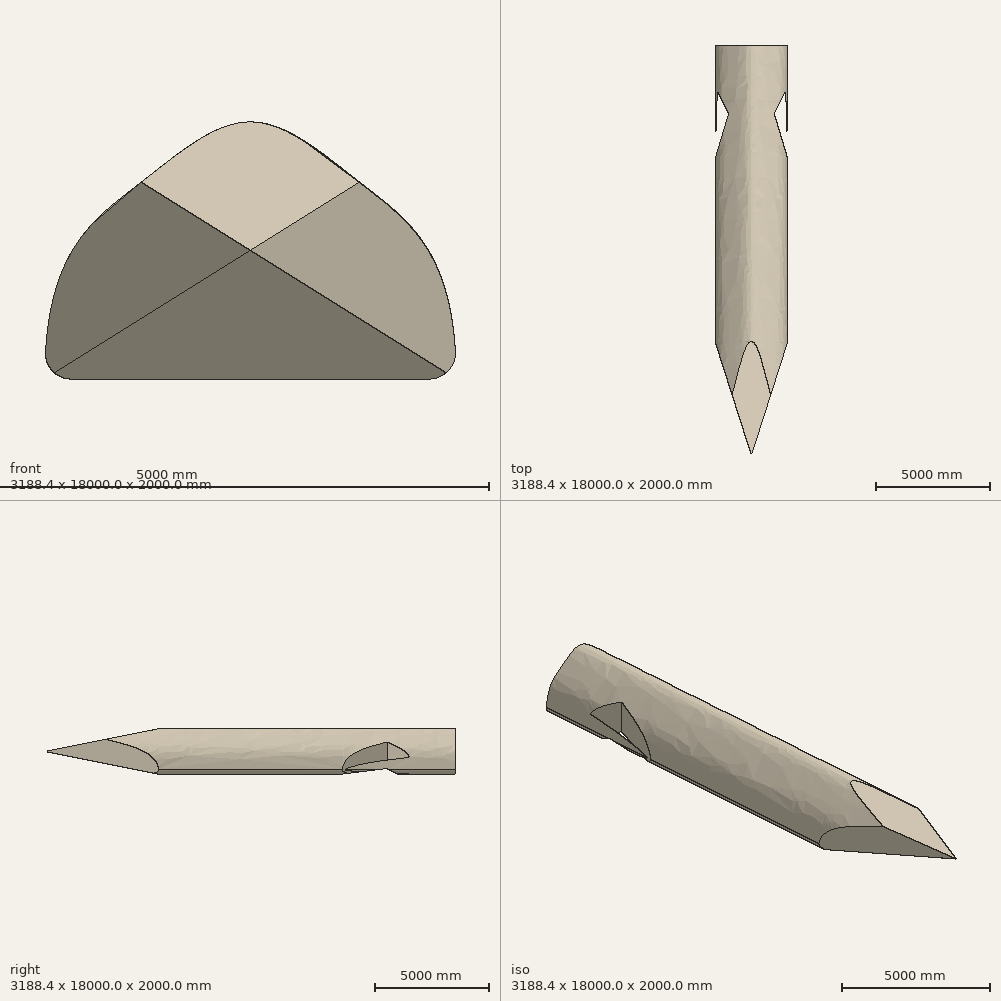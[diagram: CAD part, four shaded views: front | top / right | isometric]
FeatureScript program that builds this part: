
annotation { "Feature Type Name" : "Feature", "Feature Type Description" : "" }
export const myFeature = defineFeature(function(context is Context, id is Id, definition is map)
    precondition{}
    {
        {
            var Q0;
            Q0=qCreatedBy(makeId("Top.planeOp"),FACE);
            var sketch = newSketch(context, id + "F0", { "sketchPlane" : qUnion([Q0])});
            skPoint(sketch, "E0.middle", {"position": v(0, 0) * mm});
            skPoint(sketch, "E1.endSnap0", {"position": v(0, -4000) * mm});
            skLineSegment(sketch, "E2", {"start": v(0, -9000) * mm, "end": v(-1600, -4000) * mm});
            skLineSegment(sketch, "E3", {"start": v(1600, -4000) * mm, "end": v(0, -9000) * mm});
            skLineSegment(sketch, "E4", {"start": v(0, 4000) * mm, "end": v(0, 6000) * mm});
            skPoint(sketch, "E4.endSnap0", {"position": v(0, 4000) * mm});
            skLineSegment(sketch, "E5", {"start": v(-1000, 6000) * mm, "end": v(-1600, 4000) * mm});
            skLineSegment(sketch, "E6", {"start": v(0, 6000) * mm, "end": v(0, 7000) * mm});
            skLineSegment(sketch, "E7", {"start": v(0, 7000) * mm, "end": v(-1500, 7000) * mm});
            skLineSegment(sketch, "E8", {"start": v(-1500, 7000) * mm, "end": v(-1000, 6000) * mm});
            skLineSegment(sketch, "E9", {"start": v(1000, 6000) * mm, "end": v(1600, 4000) * mm});
            skLineSegment(sketch, "E10", {"start": v(0, 7000) * mm, "end": v(1500, 7000) * mm});
            skLineSegment(sketch, "E11", {"start": v(1500, 7000) * mm, "end": v(1000, 6000) * mm});
            skLineSegment(sketch, "E12", {"start": v(0, 7000) * mm, "end": v(0, 8000) * mm});
            skLineSegment(sketch, "E13", {"start": v(-1600, -4000) * mm, "end": v(-1600, -9000) * mm});
            skLineSegment(sketch, "E14", {"start": v(-1600, -9000) * mm, "end": v(0, -9000) * mm});
            skLineSegment(sketch, "E15", {"start": v(1600, -9000) * mm, "end": v(1600, -4000) * mm});
            skLineSegment(sketch, "E16", {"start": v(1600, -9000) * mm, "end": v(0, -9000) * mm});
            skLineSegment(sketch, "E17", {"start": v(1600, 4000) * mm, "end": v(1500, 7000) * mm});
            skLineSegment(sketch, "E18", {"start": v(-1600, 4000) * mm, "end": v(-1500, 7000) * mm});
            skSolve(sketch);
        }
        {
            var Q0;
            Q0=qCreatedBy(makeId("Right.planeOp"),FACE);
            var sketch = newSketch(context, id + "F1", { "sketchPlane" : qUnion([Q0])});
            skPoint(sketch, "E19.middle", {"position": v(0, 0) * mm});
            skLineSegment(sketch, "E20", {"start": v(-4000, -1000) * mm, "end": v(-9000, 0) * mm});
            skLineSegment(sketch, "E21", {"start": v(-9000, 0) * mm, "end": v(-4000, 1000) * mm});
            skLineSegment(sketch, "E22", {"start": v(4000, 1000) * mm, "end": v(6000, 1000) * mm});
            skLineSegment(sketch, "E23", {"start": v(4000, -1000) * mm, "end": v(6000, -750) * mm});
            skLineSegment(sketch, "E24", {"start": v(6000, 1000) * mm, "end": v(7000, 1000) * mm});
            skLineSegment(sketch, "E25", {"start": v(7000, 1000) * mm, "end": v(7000, -1250) * mm});
            skLineSegment(sketch, "E26", {"start": v(7000, -1250) * mm, "end": v(6000, -750) * mm});
            skLineSegment(sketch, "E27", {"start": v(7000, 1000) * mm, "end": v(8000, 1000) * mm});
            skLineSegment(sketch, "E28", {"start": v(-4000, -1000) * mm, "end": v(-9000, -1000) * mm});
            skLineSegment(sketch, "E29", {"start": v(-9000, -1000) * mm, "end": v(-9000, 1000) * mm});
            skLineSegment(sketch, "E30", {"start": v(-9000, 1000) * mm, "end": v(-4000, 1000) * mm});
            skLineSegment(sketch, "E31", {"start": v(4000, -1000) * mm, "end": v(7000, -1250) * mm});
            skSolve(sketch);
        }
        {
            var Q0;
            Q0=qCreatedBy(makeId("Front.planeOp"),FACE);
            var sketch = newSketch(context, id + "F2", { "sketchPlane" : qUnion([Q0])});
            skLineSegment(sketch, "E32.top", {"start": v(-1394.2, -1000) * mm, "end": v(1394.2, -1000) * mm});
            skPoint(sketch, "E32.middle", {"position": v(0, 0) * mm});
            skFitSpline(sketch, "E33", {"points": [v(-1600, -1000) * mm, v(-848, 530) * mm, v(0, 1000) * mm, v(848, 530) * mm, v(1600, -1000) * mm], "startDerivative": vector(0, 10524.75) * mm, "endDerivative": vector(0, -10524.75) * mm});
            skArc(sketch, "E34.filletArc", {"start": v(-1593.82, -787.83) * mm, "mid": v(-1539.85, -937.05) * mm, "end": v(-1394.2, -1000) * mm});
            skArc(sketch, "E35.filletArc", {"start": v(1394.2, -1000) * mm, "mid": v(1539.85, -937.05) * mm, "end": v(1593.82, -787.83) * mm});
            skSolve(sketch);
        }
        {
            var Q0;
            Q0=qSketchRegion(id+"F2",true);
            extrude(context, id + "F3", {"entities" : qUnion([Q0]), "endBound" : BoundingType.SYMMETRIC, "depth" : 18000 * mm});
        }
        {
            var Q0;
            Q0 = qSketchRegion(id + "F1", true);
            extrude(context, id + "F4", {"entities" : qUnion([Q0]), "operationType" : NewBodyOperationType.REMOVE, "endBound" : BoundingType.SYMMETRIC, "oppositeDirection" : true, "depth" : 5000 * mm});
        }
        {
            var Q0;
            Q0 = qSketchRegion(id + "F0", true);
            extrude(context, id + "F5", {"entities" : qUnion([Q0]), "operationType" : NewBodyOperationType.REMOVE, "endBound" : BoundingType.SYMMETRIC, "oppositeDirection" : true, "depth" : 10000 * mm});
        }
    });
